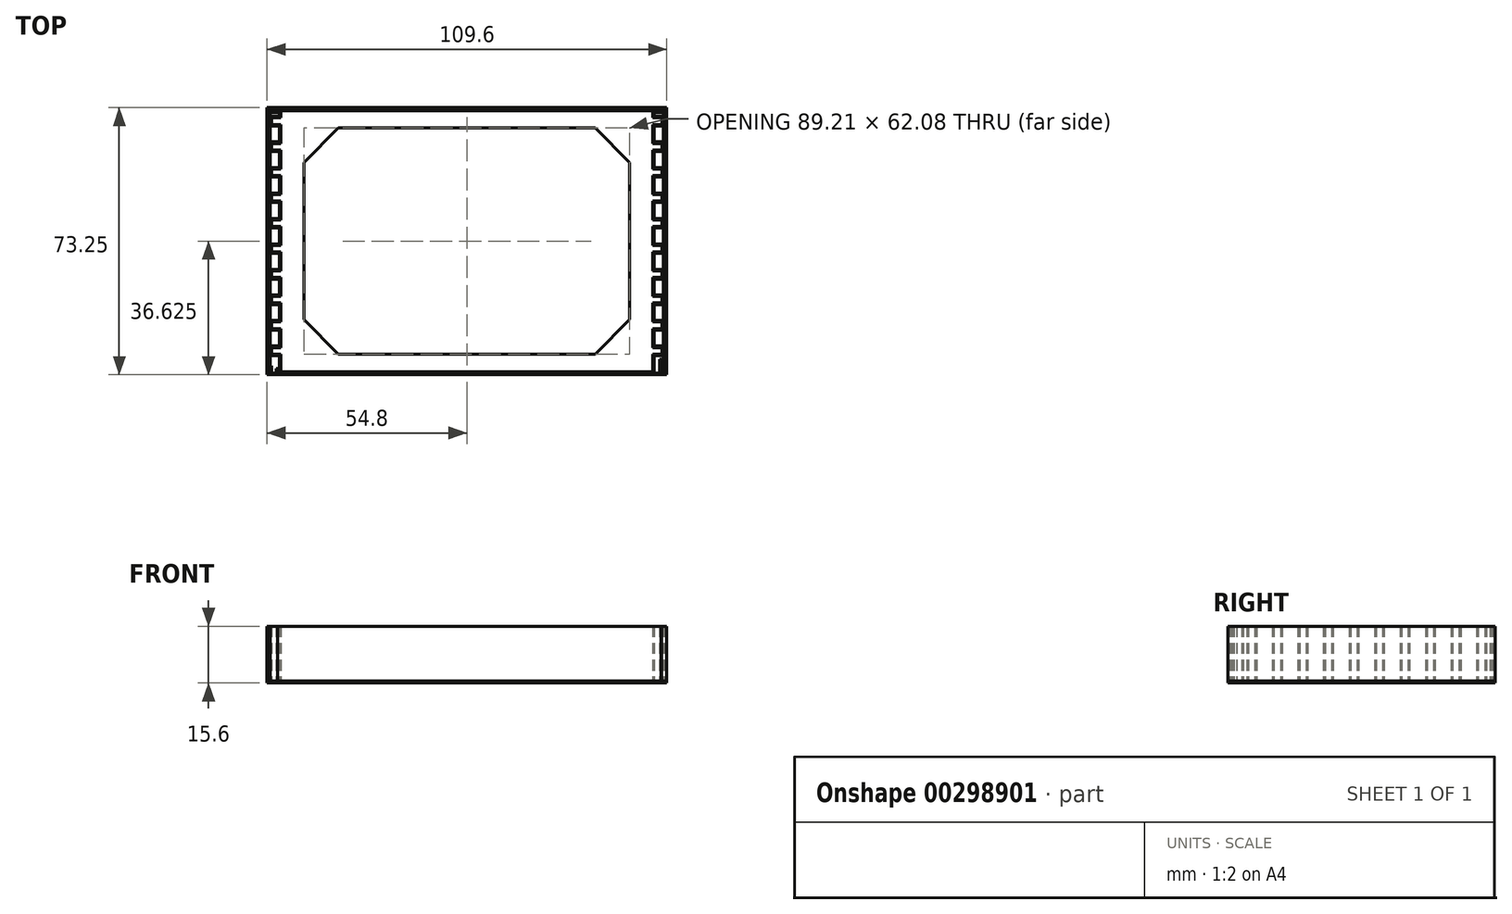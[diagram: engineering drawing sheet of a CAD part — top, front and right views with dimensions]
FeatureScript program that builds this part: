
annotation { "Feature Type Name" : "Feature", "Feature Type Description" : "" }
export const myFeature = defineFeature(function(context is Context, id is Id, definition is map)
    precondition{}
    {
        {
            var Q0;
            Q0=qCreatedBy(makeId("Top.planeOp"),FACE);
            var sketch = newSketch(context, id + "F0", { "sketchPlane" : qUnion([Q0])});
            skLineSegment(sketch, "E0", {"start": v(0, 0) * mm, "end": v(0, 4.8) * mm});
            skLineSegment(sketch, "E1", {"start": v(0, 4.8) * mm, "end": v(-2.5, 4.8) * mm});
            skLineSegment(sketch, "E2", {"start": v(-2.5, 4.8) * mm, "end": v(-2.5, 6.6) * mm});
            skLineSegment(sketch, "E3", {"start": v(-2.5, 6.6) * mm, "end": v(0, 6.6) * mm});
            skLineSegment(sketch, "E4", {"start": v(-0.4, 0) * mm, "end": v(-0.4, 4.4) * mm});
            skLineSegment(sketch, "E5", {"start": v(-0.4, 4.4) * mm, "end": v(-2.9, 4.4) * mm});
            skLineSegment(sketch, "E6", {"start": v(-2.9, 4.4) * mm, "end": v(-2.9, 7) * mm});
            skLineSegment(sketch, "E7", {"start": v(-2.9, 7) * mm, "end": v(-0.4, 7) * mm});
            skLineSegment(sketch, "E8", {"start": v(0, 6.6) * mm, "end": v(0, 7) * mm});
            skLineSegment(sketch, "E9.0.1.0", {"start": v(-2.9, 11.4) * mm, "end": v(-2.9, 14) * mm});
            skLineSegment(sketch, "E9.0.1.1", {"start": v(-0.4, 11.4) * mm, "end": v(-2.9, 11.4) * mm});
            skLineSegment(sketch, "E9.0.1.2", {"start": v(-2.5, 13.6) * mm, "end": v(0, 13.6) * mm});
            skLineSegment(sketch, "E9.0.1.3", {"start": v(0, 11.8) * mm, "end": v(-2.5, 11.8) * mm});
            skLineSegment(sketch, "E9.0.1.4", {"start": v(0, 7) * mm, "end": v(0, 11.8) * mm});
            skLineSegment(sketch, "E9.0.1.5", {"start": v(-0.4, 7) * mm, "end": v(-0.4, 11.4) * mm});
            skLineSegment(sketch, "E9.0.1.6", {"start": v(-2.9, 14) * mm, "end": v(-0.4, 14) * mm});
            skLineSegment(sketch, "E9.0.1.7", {"start": v(-2.5, 11.8) * mm, "end": v(-2.5, 13.6) * mm});
            skLineSegment(sketch, "E9.0.1.8", {"start": v(0, 13.6) * mm, "end": v(0, 14) * mm});
            skLineSegment(sketch, "E9.0.2.0", {"start": v(-2.9, 18.4) * mm, "end": v(-2.9, 21) * mm});
            skLineSegment(sketch, "E9.0.2.1", {"start": v(-0.4, 18.4) * mm, "end": v(-2.9, 18.4) * mm});
            skLineSegment(sketch, "E9.0.2.2", {"start": v(-2.5, 20.6) * mm, "end": v(0, 20.6) * mm});
            skLineSegment(sketch, "E9.0.2.3", {"start": v(0, 18.8) * mm, "end": v(-2.5, 18.8) * mm});
            skLineSegment(sketch, "E9.0.2.4", {"start": v(0, 14) * mm, "end": v(0, 18.8) * mm});
            skLineSegment(sketch, "E9.0.2.5", {"start": v(-0.4, 14) * mm, "end": v(-0.4, 18.4) * mm});
            skLineSegment(sketch, "E9.0.2.6", {"start": v(-2.9, 21) * mm, "end": v(-0.4, 21) * mm});
            skLineSegment(sketch, "E9.0.2.7", {"start": v(-2.5, 18.8) * mm, "end": v(-2.5, 20.6) * mm});
            skLineSegment(sketch, "E9.0.2.8", {"start": v(0, 20.6) * mm, "end": v(0, 21) * mm});
            skLineSegment(sketch, "E9.0.3.0", {"start": v(-2.9, 25.4) * mm, "end": v(-2.9, 28) * mm});
            skLineSegment(sketch, "E9.0.3.1", {"start": v(-0.4, 25.4) * mm, "end": v(-2.9, 25.4) * mm});
            skLineSegment(sketch, "E9.0.3.2", {"start": v(-2.5, 27.6) * mm, "end": v(0, 27.6) * mm});
            skLineSegment(sketch, "E9.0.3.3", {"start": v(0, 25.8) * mm, "end": v(-2.5, 25.8) * mm});
            skLineSegment(sketch, "E9.0.3.4", {"start": v(0, 21) * mm, "end": v(0, 25.8) * mm});
            skLineSegment(sketch, "E9.0.3.5", {"start": v(-0.4, 21) * mm, "end": v(-0.4, 25.4) * mm});
            skLineSegment(sketch, "E9.0.3.6", {"start": v(-2.9, 28) * mm, "end": v(-0.4, 28) * mm});
            skLineSegment(sketch, "E9.0.3.7", {"start": v(-2.5, 25.8) * mm, "end": v(-2.5, 27.6) * mm});
            skLineSegment(sketch, "E9.0.3.8", {"start": v(0, 27.6) * mm, "end": v(0, 28) * mm});
            skLineSegment(sketch, "E9.0.4.0", {"start": v(-2.9, 32.4) * mm, "end": v(-2.9, 35) * mm});
            skLineSegment(sketch, "E9.0.4.1", {"start": v(-0.4, 32.4) * mm, "end": v(-2.9, 32.4) * mm});
            skLineSegment(sketch, "E9.0.4.2", {"start": v(-2.5, 34.6) * mm, "end": v(0, 34.6) * mm});
            skLineSegment(sketch, "E9.0.4.3", {"start": v(0, 32.8) * mm, "end": v(-2.5, 32.8) * mm});
            skLineSegment(sketch, "E9.0.4.4", {"start": v(0, 28) * mm, "end": v(0, 32.8) * mm});
            skLineSegment(sketch, "E9.0.4.5", {"start": v(-0.4, 28) * mm, "end": v(-0.4, 32.4) * mm});
            skLineSegment(sketch, "E9.0.4.6", {"start": v(-2.9, 35) * mm, "end": v(-0.4, 35) * mm});
            skLineSegment(sketch, "E9.0.4.7", {"start": v(-2.5, 32.8) * mm, "end": v(-2.5, 34.6) * mm});
            skLineSegment(sketch, "E9.0.4.8", {"start": v(0, 34.6) * mm, "end": v(0, 35) * mm});
            skLineSegment(sketch, "E9.0.5.0", {"start": v(-2.9, 39.4) * mm, "end": v(-2.9, 42) * mm});
            skLineSegment(sketch, "E9.0.5.1", {"start": v(-0.4, 39.4) * mm, "end": v(-2.9, 39.4) * mm});
            skLineSegment(sketch, "E9.0.5.2", {"start": v(-2.5, 41.6) * mm, "end": v(0, 41.6) * mm});
            skLineSegment(sketch, "E9.0.5.3", {"start": v(0, 39.8) * mm, "end": v(-2.5, 39.8) * mm});
            skLineSegment(sketch, "E9.0.5.4", {"start": v(0, 35) * mm, "end": v(0, 39.8) * mm});
            skLineSegment(sketch, "E9.0.5.5", {"start": v(-0.4, 35) * mm, "end": v(-0.4, 39.4) * mm});
            skLineSegment(sketch, "E9.0.5.6", {"start": v(-2.9, 42) * mm, "end": v(-0.4, 42) * mm});
            skLineSegment(sketch, "E9.0.5.7", {"start": v(-2.5, 39.8) * mm, "end": v(-2.5, 41.6) * mm});
            skLineSegment(sketch, "E9.0.5.8", {"start": v(0, 41.6) * mm, "end": v(0, 42) * mm});
            skLineSegment(sketch, "E9.0.6.0", {"start": v(-2.9, 46.4) * mm, "end": v(-2.9, 49) * mm});
            skLineSegment(sketch, "E9.0.6.1", {"start": v(-0.4, 46.4) * mm, "end": v(-2.9, 46.4) * mm});
            skLineSegment(sketch, "E9.0.6.2", {"start": v(-2.5, 48.6) * mm, "end": v(0, 48.6) * mm});
            skLineSegment(sketch, "E9.0.6.3", {"start": v(0, 46.8) * mm, "end": v(-2.5, 46.8) * mm});
            skLineSegment(sketch, "E9.0.6.4", {"start": v(0, 42) * mm, "end": v(0, 46.8) * mm});
            skLineSegment(sketch, "E9.0.6.5", {"start": v(-0.4, 42) * mm, "end": v(-0.4, 46.4) * mm});
            skLineSegment(sketch, "E9.0.6.6", {"start": v(-2.9, 49) * mm, "end": v(-0.4, 49) * mm});
            skLineSegment(sketch, "E9.0.6.7", {"start": v(-2.5, 46.8) * mm, "end": v(-2.5, 48.6) * mm});
            skLineSegment(sketch, "E9.0.6.8", {"start": v(0, 48.6) * mm, "end": v(0, 49) * mm});
            skLineSegment(sketch, "E9.0.7.0", {"start": v(-2.9, 53.4) * mm, "end": v(-2.9, 56) * mm});
            skLineSegment(sketch, "E9.0.7.1", {"start": v(-0.4, 53.4) * mm, "end": v(-2.9, 53.4) * mm});
            skLineSegment(sketch, "E9.0.7.2", {"start": v(-2.5, 55.6) * mm, "end": v(0, 55.6) * mm});
            skLineSegment(sketch, "E9.0.7.3", {"start": v(0, 53.8) * mm, "end": v(-2.5, 53.8) * mm});
            skLineSegment(sketch, "E9.0.7.4", {"start": v(0, 49) * mm, "end": v(0, 53.8) * mm});
            skLineSegment(sketch, "E9.0.7.5", {"start": v(-0.4, 49) * mm, "end": v(-0.4, 53.4) * mm});
            skLineSegment(sketch, "E9.0.7.6", {"start": v(-2.9, 56) * mm, "end": v(-0.4, 56) * mm});
            skLineSegment(sketch, "E9.0.7.7", {"start": v(-2.5, 53.8) * mm, "end": v(-2.5, 55.6) * mm});
            skLineSegment(sketch, "E9.0.7.8", {"start": v(0, 55.6) * mm, "end": v(0, 56) * mm});
            skLineSegment(sketch, "E9.0.8.0", {"start": v(-2.9, 60.4) * mm, "end": v(-2.9, 63) * mm});
            skLineSegment(sketch, "E9.0.8.1", {"start": v(-0.4, 60.4) * mm, "end": v(-2.9, 60.4) * mm});
            skLineSegment(sketch, "E9.0.8.2", {"start": v(-2.5, 62.6) * mm, "end": v(0, 62.6) * mm});
            skLineSegment(sketch, "E9.0.8.3", {"start": v(0, 60.8) * mm, "end": v(-2.5, 60.8) * mm});
            skLineSegment(sketch, "E9.0.8.4", {"start": v(0, 56) * mm, "end": v(0, 60.8) * mm});
            skLineSegment(sketch, "E9.0.8.5", {"start": v(-0.4, 56) * mm, "end": v(-0.4, 60.4) * mm});
            skLineSegment(sketch, "E9.0.8.6", {"start": v(-2.9, 63) * mm, "end": v(-0.4, 63) * mm});
            skLineSegment(sketch, "E9.0.8.7", {"start": v(-2.5, 60.8) * mm, "end": v(-2.5, 62.6) * mm});
            skLineSegment(sketch, "E9.0.8.8", {"start": v(0, 62.6) * mm, "end": v(0, 63) * mm});
            skLineSegment(sketch, "E9.direction1", {"start": v(-0.4, 0) * mm, "end": v(-14.5, 0) * mm, "construction": true});
            skLineSegment(sketch, "E9.direction2", {"start": v(-0.4, 0) * mm, "end": v(-0.4, 7) * mm, "construction": true});
            skLineSegment(sketch, "E10.0.0.9", {"start": v(-2.9, 67.4) * mm, "end": v(-2.9, 70) * mm});
            skLineSegment(sketch, "E10.3.0.9", {"start": v(-0.4, 67.4) * mm, "end": v(-2.9, 67.4) * mm});
            skLineSegment(sketch, "E10.6.0.9", {"start": v(-2.5, 69.6) * mm, "end": v(0, 69.6) * mm});
            skLineSegment(sketch, "E10.9.0.9", {"start": v(0, 67.8) * mm, "end": v(-2.5, 67.8) * mm});
            skLineSegment(sketch, "E10.12.0.9", {"start": v(0, 63) * mm, "end": v(0, 67.8) * mm});
            skLineSegment(sketch, "E10.15.0.9", {"start": v(-0.4, 63) * mm, "end": v(-0.4, 67.4) * mm});
            skLineSegment(sketch, "E10.18.0.9", {"start": v(-2.9, 70) * mm, "end": v(-0.4, 70) * mm});
            skLineSegment(sketch, "E10.21.0.9", {"start": v(-2.5, 67.8) * mm, "end": v(-2.5, 69.6) * mm});
            skLineSegment(sketch, "E10.24.0.9", {"start": v(0, 69.6) * mm, "end": v(0, 70) * mm});
            skLineSegment(sketch, "E11", {"start": v(0, 70) * mm, "end": v(0, 71.5) * mm});
            skLineSegment(sketch, "E12", {"start": v(0, 71.5) * mm, "end": v(-2.9, 71.5) * mm});
            skLineSegment(sketch, "E13", {"start": v(-2.9, 71.5) * mm, "end": v(-2.9, 71.1) * mm});
            skLineSegment(sketch, "E14", {"start": v(-2.9, 71.1) * mm, "end": v(-0.4, 71.1) * mm});
            skLineSegment(sketch, "E15", {"start": v(-0.4, 71.1) * mm, "end": v(-0.4, 70) * mm});
            skLineSegment(sketch, "E16", {"start": v(-2.95, 71.55) * mm, "end": v(-2.95, 3.4) * mm});
            skLineSegment(sketch, "E17", {"start": v(-2.95, 71.55) * mm, "end": v(51, 71.55) * mm});
            skLineSegment(sketch, "E18", {"start": v(51, 71.95) * mm, "end": v(-3.35, 71.95) * mm});
            skLineSegment(sketch, "E19", {"start": v(-3.35, 71.95) * mm, "end": v(-3.35, -0.45) * mm});
            skLineSegment(sketch, "E20", {"start": v(-0.4, 0) * mm, "end": v(-0.4, -0.4) * mm});
            skLineSegment(sketch, "E21", {"start": v(-0.4, -0.4) * mm, "end": v(51, -0.4) * mm});
            skLineSegment(sketch, "E22", {"start": v(0, 0) * mm, "end": v(51, 0) * mm});
            skLineSegment(sketch, "E23", {"start": v(51, 71.55) * mm, "end": v(51, 0) * mm, "construction": true});
            skLineSegment(sketch, "E24.MirrorCS", {"start": v(102.4, 0) * mm, "end": v(102.4, -0.4) * mm});
            skLineSegment(sketch, "E25.MirrorCS", {"start": v(104.9, 71.5) * mm, "end": v(104.9, 71.1) * mm});
            skLineSegment(sketch, "E26.MirrorCS", {"start": v(102, 6.6) * mm, "end": v(102, 7) * mm});
            skLineSegment(sketch, "E27.MirrorCS", {"start": v(102, 34.6) * mm, "end": v(102, 35) * mm});
            skLineSegment(sketch, "E28.MirrorCS", {"start": v(104.5, 25.8) * mm, "end": v(104.5, 27.6) * mm});
            skLineSegment(sketch, "E29.MirrorCS", {"start": v(102, 27.6) * mm, "end": v(102, 28) * mm});
            skLineSegment(sketch, "E30.MirrorCS", {"start": v(104.5, 62.6) * mm, "end": v(102, 62.6) * mm});
            skLineSegment(sketch, "E31.MirrorCS", {"start": v(104.9, 70) * mm, "end": v(102.4, 70) * mm});
            skLineSegment(sketch, "E32.MirrorCS", {"start": v(104.9, 71.1) * mm, "end": v(102.4, 71.1) * mm});
            skLineSegment(sketch, "E33.MirrorCS", {"start": v(104.9, 28) * mm, "end": v(102.4, 28) * mm});
            skLineSegment(sketch, "E34.MirrorCS", {"start": v(104.5, 53.8) * mm, "end": v(104.5, 55.6) * mm});
            skLineSegment(sketch, "E35.MirrorCS", {"start": v(104.5, 60.8) * mm, "end": v(104.5, 62.6) * mm});
            skLineSegment(sketch, "E36.MirrorCS", {"start": v(104.5, 4.8) * mm, "end": v(104.5, 6.6) * mm});
            skLineSegment(sketch, "E37.MirrorCS", {"start": v(102, 4.8) * mm, "end": v(104.5, 4.8) * mm});
            skLineSegment(sketch, "E38.MirrorCS", {"start": v(104.9, 25.4) * mm, "end": v(104.9, 28) * mm});
            skLineSegment(sketch, "E39.MirrorCS", {"start": v(102, 69.6) * mm, "end": v(102, 70) * mm});
            skLineSegment(sketch, "E40.MirrorCS", {"start": v(102.4, 4.4) * mm, "end": v(104.9, 4.4) * mm});
            skLineSegment(sketch, "E41.MirrorCS", {"start": v(104.5, 46.8) * mm, "end": v(104.5, 48.6) * mm});
            skLineSegment(sketch, "E42.MirrorCS", {"start": v(102.4, 71.1) * mm, "end": v(102.4, 70) * mm});
            skLineSegment(sketch, "E43.MirrorCS", {"start": v(104.5, 27.6) * mm, "end": v(102, 27.6) * mm});
            skLineSegment(sketch, "E44.MirrorCS", {"start": v(102, 55.6) * mm, "end": v(102, 56) * mm});
            skLineSegment(sketch, "E45.MirrorCS", {"start": v(102, 71.5) * mm, "end": v(104.9, 71.5) * mm});
            skLineSegment(sketch, "E46.MirrorCS", {"start": v(102, 62.6) * mm, "end": v(102, 63) * mm});
            skLineSegment(sketch, "E47.MirrorCS", {"start": v(102, 70) * mm, "end": v(102, 71.5) * mm});
            skLineSegment(sketch, "E48.MirrorCS", {"start": v(104.9, 63) * mm, "end": v(102.4, 63) * mm});
            skLineSegment(sketch, "E49.MirrorCS", {"start": v(104.9, 60.4) * mm, "end": v(104.9, 63) * mm});
            skLineSegment(sketch, "E50.MirrorCS", {"start": v(102, 53.8) * mm, "end": v(104.5, 53.8) * mm});
            skLineSegment(sketch, "E51.MirrorCS", {"start": v(104.5, 67.8) * mm, "end": v(104.5, 69.6) * mm});
            skLineSegment(sketch, "E52.MirrorCS", {"start": v(104.9, 18.4) * mm, "end": v(104.9, 21) * mm});
            skLineSegment(sketch, "E53.MirrorCS", {"start": v(102.4, 60.4) * mm, "end": v(104.9, 60.4) * mm});
            skLineSegment(sketch, "E54.MirrorCS", {"start": v(104.9, 67.4) * mm, "end": v(104.9, 70) * mm});
            skLineSegment(sketch, "E55.MirrorCS", {"start": v(104.5, 18.8) * mm, "end": v(104.5, 20.6) * mm});
            skLineSegment(sketch, "E56.MirrorCS", {"start": v(102, 46.8) * mm, "end": v(104.5, 46.8) * mm});
            skLineSegment(sketch, "E57.MirrorCS", {"start": v(104.9, 14) * mm, "end": v(102.4, 14) * mm});
            skLineSegment(sketch, "E58.MirrorCS", {"start": v(104.5, 34.6) * mm, "end": v(102, 34.6) * mm});
            skLineSegment(sketch, "E59.MirrorCS", {"start": v(102.4, 18.4) * mm, "end": v(104.9, 18.4) * mm});
            skLineSegment(sketch, "E60.MirrorCS", {"start": v(104.9, 46.4) * mm, "end": v(104.9, 49) * mm});
            skLineSegment(sketch, "E61.MirrorCS", {"start": v(104.5, 41.6) * mm, "end": v(102, 41.6) * mm});
            skLineSegment(sketch, "E62.MirrorCS", {"start": v(104.9, 53.4) * mm, "end": v(104.9, 56) * mm});
            skLineSegment(sketch, "E63.MirrorCS", {"start": v(102, 67.8) * mm, "end": v(104.5, 67.8) * mm});
            skLineSegment(sketch, "E64.MirrorCS", {"start": v(102.4, 0) * mm, "end": v(102.4, 4.4) * mm});
            skLineSegment(sketch, "E65.MirrorCS", {"start": v(104.5, 6.6) * mm, "end": v(102, 6.6) * mm});
            skLineSegment(sketch, "E66.MirrorCS", {"start": v(102.4, 0) * mm, "end": v(116.5, 0) * mm, "construction": true});
            skLineSegment(sketch, "E67.MirrorCS", {"start": v(104.5, 55.6) * mm, "end": v(102, 55.6) * mm});
            skLineSegment(sketch, "E68.MirrorCS", {"start": v(104.5, 32.8) * mm, "end": v(104.5, 34.6) * mm});
            skLineSegment(sketch, "E69.MirrorCS", {"start": v(102, 60.8) * mm, "end": v(104.5, 60.8) * mm});
            skLineSegment(sketch, "E70.MirrorCS", {"start": v(104.5, 20.6) * mm, "end": v(102, 20.6) * mm});
            skLineSegment(sketch, "E71.MirrorCS", {"start": v(102.4, 67.4) * mm, "end": v(104.9, 67.4) * mm});
            skLineSegment(sketch, "E72.MirrorCS", {"start": v(104.5, 39.8) * mm, "end": v(104.5, 41.6) * mm});
            skLineSegment(sketch, "E73.MirrorCS", {"start": v(104.9, 39.4) * mm, "end": v(104.9, 42) * mm});
            skLineSegment(sketch, "E74.MirrorCS", {"start": v(104.9, 4.4) * mm, "end": v(104.9, 7) * mm});
            skLineSegment(sketch, "E75.MirrorCS", {"start": v(104.9, 7) * mm, "end": v(102.4, 7) * mm});
            skLineSegment(sketch, "E76.MirrorCS", {"start": v(104.9, 11.4) * mm, "end": v(104.9, 14) * mm});
            skLineSegment(sketch, "E77.MirrorCS", {"start": v(102.4, 11.4) * mm, "end": v(104.9, 11.4) * mm});
            skLineSegment(sketch, "E78.MirrorCS", {"start": v(102, 20.6) * mm, "end": v(102, 21) * mm});
            skLineSegment(sketch, "E79.MirrorCS", {"start": v(104.5, 13.6) * mm, "end": v(102, 13.6) * mm});
            skLineSegment(sketch, "E80.MirrorCS", {"start": v(102, 11.8) * mm, "end": v(104.5, 11.8) * mm});
            skLineSegment(sketch, "E81.MirrorCS", {"start": v(102, 32.8) * mm, "end": v(104.5, 32.8) * mm});
            skLineSegment(sketch, "E82.MirrorCS", {"start": v(104.9, 32.4) * mm, "end": v(104.9, 35) * mm});
            skLineSegment(sketch, "E83.MirrorCS", {"start": v(102.4, 46.4) * mm, "end": v(104.9, 46.4) * mm});
            skLineSegment(sketch, "E84.MirrorCS", {"start": v(104.5, 11.8) * mm, "end": v(104.5, 13.6) * mm});
            skLineSegment(sketch, "E85.MirrorCS", {"start": v(102.4, 53.4) * mm, "end": v(104.9, 53.4) * mm});
            skLineSegment(sketch, "E86.MirrorCS", {"start": v(102, 39.8) * mm, "end": v(104.5, 39.8) * mm});
            skLineSegment(sketch, "E87.MirrorCS", {"start": v(104.9, 49) * mm, "end": v(102.4, 49) * mm});
            skLineSegment(sketch, "E88.MirrorCS", {"start": v(102.4, 25.4) * mm, "end": v(104.9, 25.4) * mm});
            skLineSegment(sketch, "E89.MirrorCS", {"start": v(102, 18.8) * mm, "end": v(104.5, 18.8) * mm});
            skLineSegment(sketch, "E90.MirrorCS", {"start": v(104.9, 56) * mm, "end": v(102.4, 56) * mm});
            skLineSegment(sketch, "E91.MirrorCS", {"start": v(104.5, 69.6) * mm, "end": v(102, 69.6) * mm});
            skLineSegment(sketch, "E92.MirrorCS", {"start": v(102, 48.6) * mm, "end": v(102, 49) * mm});
            skLineSegment(sketch, "E93.MirrorCS", {"start": v(102, 41.6) * mm, "end": v(102, 42) * mm});
            skLineSegment(sketch, "E94.MirrorCS", {"start": v(102.4, 39.4) * mm, "end": v(104.9, 39.4) * mm});
            skLineSegment(sketch, "E95.MirrorCS", {"start": v(102, 25.8) * mm, "end": v(104.5, 25.8) * mm});
            skLineSegment(sketch, "E96.MirrorCS", {"start": v(102.4, 32.4) * mm, "end": v(104.9, 32.4) * mm});
            skLineSegment(sketch, "E97.MirrorCS", {"start": v(104.5, 48.6) * mm, "end": v(102, 48.6) * mm});
            skLineSegment(sketch, "E98.MirrorCS", {"start": v(104.9, 35) * mm, "end": v(102.4, 35) * mm});
            skLineSegment(sketch, "E99.MirrorCS", {"start": v(104.9, 21) * mm, "end": v(102.4, 21) * mm});
            skLineSegment(sketch, "E100.MirrorCS", {"start": v(104.9, 42) * mm, "end": v(102.4, 42) * mm});
            skLineSegment(sketch, "E101.MirrorCS", {"start": v(102, 13.6) * mm, "end": v(102, 14) * mm});
            skLineSegment(sketch, "E102.MirrorCS", {"start": v(102.4, 0) * mm, "end": v(102.4, 7) * mm, "construction": true});
            skLineSegment(sketch, "E103.MirrorCS", {"start": v(102, 0) * mm, "end": v(102, 4.8) * mm});
            skLineSegment(sketch, "E104.MirrorCS", {"start": v(102.4, 35) * mm, "end": v(102.4, 39.4) * mm});
            skLineSegment(sketch, "E105.MirrorCS", {"start": v(102, 42) * mm, "end": v(102, 46.8) * mm});
            skLineSegment(sketch, "E106.MirrorCS", {"start": v(51, 71.95) * mm, "end": v(105.35, 71.95) * mm});
            skLineSegment(sketch, "E107.MirrorCS", {"start": v(102.4, 28) * mm, "end": v(102.4, 32.4) * mm});
            skLineSegment(sketch, "E108.MirrorCS", {"start": v(102.4, 7) * mm, "end": v(102.4, 11.4) * mm});
            skLineSegment(sketch, "E109.MirrorCS", {"start": v(102, 7) * mm, "end": v(102, 11.8) * mm});
            skLineSegment(sketch, "E110.MirrorCS", {"start": v(104.95, 71.55) * mm, "end": v(51, 71.55) * mm});
            skLineSegment(sketch, "E111.MirrorCS", {"start": v(102.4, -0.4) * mm, "end": v(51, -0.4) * mm});
            skLineSegment(sketch, "E112.MirrorCS", {"start": v(104.95, 71.55) * mm, "end": v(104.95, 3.4) * mm});
            skLineSegment(sketch, "E113.MirrorCS", {"start": v(102, 35) * mm, "end": v(102, 39.8) * mm});
            skLineSegment(sketch, "E114.MirrorCS", {"start": v(102, 21) * mm, "end": v(102, 25.8) * mm});
            skLineSegment(sketch, "E115.MirrorCS", {"start": v(102, 14) * mm, "end": v(102, 18.8) * mm});
            skLineSegment(sketch, "E116.MirrorCS", {"start": v(102.4, 42) * mm, "end": v(102.4, 46.4) * mm});
            skLineSegment(sketch, "E117.MirrorCS", {"start": v(102.4, 56) * mm, "end": v(102.4, 60.4) * mm});
            skLineSegment(sketch, "E118.MirrorCS", {"start": v(102.4, 49) * mm, "end": v(102.4, 53.4) * mm});
            skLineSegment(sketch, "E119.MirrorCS", {"start": v(102, 49) * mm, "end": v(102, 53.8) * mm});
            skLineSegment(sketch, "E120.MirrorCS", {"start": v(105.35, 71.95) * mm, "end": v(105.35, 3) * mm});
            skLineSegment(sketch, "E121.MirrorCS", {"start": v(102.4, 14) * mm, "end": v(102.4, 18.4) * mm});
            skLineSegment(sketch, "E122.MirrorCS", {"start": v(102, 63) * mm, "end": v(102, 67.8) * mm});
            skLineSegment(sketch, "E123.MirrorCS", {"start": v(102, 0) * mm, "end": v(51, 0) * mm});
            skLineSegment(sketch, "E124.MirrorCS", {"start": v(102, 56) * mm, "end": v(102, 60.8) * mm});
            skLineSegment(sketch, "E125.MirrorCS", {"start": v(102.4, 21) * mm, "end": v(102.4, 25.4) * mm});
            skLineSegment(sketch, "E126.MirrorCS", {"start": v(102.4, 63) * mm, "end": v(102.4, 67.4) * mm});
            skLineSegment(sketch, "E127.MirrorCS", {"start": v(102, 28) * mm, "end": v(102, 32.8) * mm});
            skLineSegment(sketch, "E128", {"start": v(-0.45, 0) * mm, "end": v(-0.45, -0.45) * mm});
            skLineSegment(sketch, "E129", {"start": v(-0.85, 0.45) * mm, "end": v(-0.85, -0.85) * mm});
            skLineSegment(sketch, "E130", {"start": v(-0.85, -0.85) * mm, "end": v(104.3, -0.85) * mm});
            skLineSegment(sketch, "E131", {"start": v(-0.45, -0.45) * mm, "end": v(103.9, -0.45) * mm});
            skLineSegment(sketch, "E132", {"start": v(-2.95, 3.4) * mm, "end": v(-2.95, -0.85) * mm});
            skLineSegment(sketch, "E133", {"start": v(-2.95, -0.85) * mm, "end": v(-3.8, -0.85) * mm});
            skLineSegment(sketch, "E134", {"start": v(-3.35, -0.45) * mm, "end": v(-3.4, -0.45) * mm});
            skLineSegment(sketch, "E135", {"start": v(-3.4, -0.45) * mm, "end": v(-3.4, 72) * mm});
            skLineSegment(sketch, "E136", {"start": v(-3.8, -0.85) * mm, "end": v(-3.8, 72.4) * mm});
            skLineSegment(sketch, "E137", {"start": v(-3.4, 72) * mm, "end": v(105.4, 72) * mm});
            skLineSegment(sketch, "E138", {"start": v(-3.8, 72.4) * mm, "end": v(105.8, 72.4) * mm});
            skLineSegment(sketch, "E139", {"start": v(105.4, 72) * mm, "end": v(105.4, 0) * mm});
            skLineSegment(sketch, "E140", {"start": v(103.9, -0.45) * mm, "end": v(103.9, 3) * mm});
            skLineSegment(sketch, "E141", {"start": v(105.8, 72.4) * mm, "end": v(105.8, -0.85) * mm});
            skLineSegment(sketch, "E142", {"start": v(104.95, 3.4) * mm, "end": v(103.9, 3.4) * mm});
            skLineSegment(sketch, "E143", {"start": v(103.9, 3.4) * mm, "end": v(103.9, 3) * mm});
            skLineSegment(sketch, "E144", {"start": v(105.35, 3) * mm, "end": v(104.3, 3) * mm});
            skLineSegment(sketch, "E145", {"start": v(104.3, 3) * mm, "end": v(104.3, -0.85) * mm});
            skLineSegment(sketch, "E146", {"start": v(105.8, -0.85) * mm, "end": v(104.35, -0.85) * mm});
            skLineSegment(sketch, "E147", {"start": v(104.35, -0.85) * mm, "end": v(104.35, 2.95) * mm});
            skLineSegment(sketch, "E148", {"start": v(105.4, 0) * mm, "end": v(105.4, -0.45) * mm});
            skLineSegment(sketch, "E149", {"start": v(105.4, -0.45) * mm, "end": v(104.75, -0.45) * mm});
            skLineSegment(sketch, "E150", {"start": v(104.75, -0.45) * mm, "end": v(104.75, 2.95) * mm});
            skLineSegment(sketch, "E151", {"start": v(104.75, 2.95) * mm, "end": v(104.35, 2.95) * mm});
            skLineSegment(sketch, "E152", {"start": v(-0.45, 0) * mm, "end": v(-0.45, 0.85) * mm});
            skLineSegment(sketch, "E153", {"start": v(-0.45, 0.85) * mm, "end": v(-1.3, 0.85) * mm});
            skLineSegment(sketch, "E154", {"start": v(-1.3, 0.85) * mm, "end": v(-1.3, -0.45) * mm});
            skLineSegment(sketch, "E155", {"start": v(-1.3, -0.45) * mm, "end": v(-2.5, -0.45) * mm});
            skLineSegment(sketch, "E156", {"start": v(-0.85, 0.45) * mm, "end": v(-0.9, 0.45) * mm});
            skLineSegment(sketch, "E157", {"start": v(-0.9, 0.45) * mm, "end": v(-0.9, -0.85) * mm});
            skLineSegment(sketch, "E158", {"start": v(-0.9, -0.85) * mm, "end": v(-2.9, -0.85) * mm});
            skLineSegment(sketch, "E159", {"start": v(-2.9, -0.85) * mm, "end": v(-2.9, 1.61) * mm});
            skLineSegment(sketch, "E160", {"start": v(-2.9, 1.61) * mm, "end": v(-2.5, 1.61) * mm});
            skLineSegment(sketch, "E161", {"start": v(-2.5, 1.61) * mm, "end": v(-2.5, -0.45) * mm});
            skSolve(sketch);
        }
        {
            var Q0;
            Q0 = qSketchRegion(id + "F0", true);
            extrude(context, id + "F1", {"entities" : qUnion([Q0]), "depth" : 15 * mm});
        }
        {
            var Q0;
            Q0=qCreatedBy(makeId("Top.planeOp"),FACE);
            var sketch = newSketch(context, id + "F2", { "sketchPlane" : qUnion([Q0])});
            skLineSegment(sketch, "E162", {"start": v(51, 72.4) * mm, "end": v(51, -0.85) * mm, "construction": true});
            skLineSegment(sketch, "E163", {"start": v(-2.86, 35.78) * mm, "end": v(104.86, 35.78) * mm, "construction": true});
            skLineSegment(sketch, "E164.bottom", {"start": v(15.75, 66.81) * mm, "end": v(86.25, 66.81) * mm});
            skLineSegment(sketch, "E164.top", {"start": v(15.75, 4.74) * mm, "end": v(86.25, 4.74) * mm});
            skLineSegment(sketch, "E164.left", {"start": v(6.4, 57.31) * mm, "end": v(6.4, 14.24) * mm});
            skLineSegment(sketch, "E164.right", {"start": v(95.6, 57.31) * mm, "end": v(95.6, 14.24) * mm});
            skPoint(sketch, "E164.middle", {"position": v(51, 35.78) * mm});
            skPoint(sketch, "E165.0.midPoint", {"position": v(15.75, 66.81) * mm});
            skLineSegment(sketch, "E166", {"start": v(15.75, 66.81) * mm, "end": v(6.4, 57.31) * mm});
            skLineSegment(sketch, "E167.MirrorCS", {"start": v(86.25, 66.81) * mm, "end": v(95.6, 57.31) * mm});
            skLineSegment(sketch, "E168.MirrorCS", {"start": v(15.75, 4.74) * mm, "end": v(6.4, 14.24) * mm});
            skLineSegment(sketch, "E169.MirrorCS", {"start": v(86.25, 4.74) * mm, "end": v(95.6, 14.24) * mm});
            skPoint(sketch, "E170.orphan", {"position": v(6.4, 66.81) * mm});
            skPoint(sketch, "E171.orphan", {"position": v(6.4, 4.74) * mm});
            skPoint(sketch, "E172.orphan", {"position": v(95.6, 4.74) * mm});
            skPoint(sketch, "E173.orphan", {"position": v(95.6, 66.81) * mm});
            skLineSegment(sketch, "E174.bottom", {"start": v(-3.8, 72.4) * mm, "end": v(105.8, 72.4) * mm});
            skLineSegment(sketch, "E174.top", {"start": v(-3.8, -0.85) * mm, "end": v(105.8, -0.85) * mm});
            skLineSegment(sketch, "E174.left", {"start": v(-3.8, 72.4) * mm, "end": v(-3.8, -0.85) * mm});
            skLineSegment(sketch, "E174.right", {"start": v(105.8, 72.4) * mm, "end": v(105.8, -0.85) * mm});
            skSolve(sketch);
        }
        {
            var Q0;
            Q0 = qSketchRegion(id + "F2", true);
            extrude(context, id + "F3", {"entities" : qUnion([Q0]), "oppositeDirection" : true, "depth" : 0.6 * mm});
        }
    });
